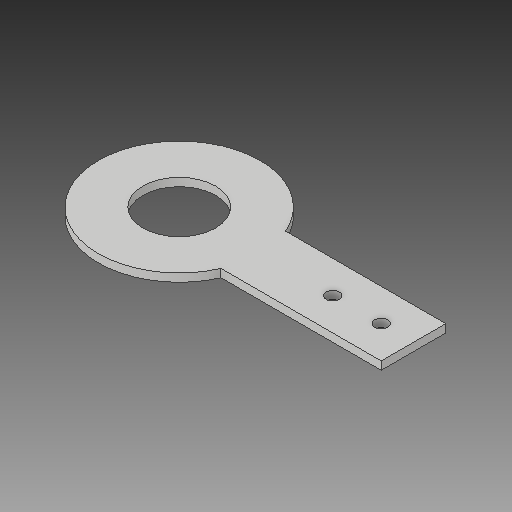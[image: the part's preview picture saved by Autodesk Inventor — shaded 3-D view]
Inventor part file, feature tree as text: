
AUTODESK INVENTOR PART (.ipt)
format: ipt  version: 2018 (Build 220112000, 112)  size: 98,816 bytes
history: native  units: in
note: dims shown in document units (in); Inventor stores cm internally (conversion verified against a paired STEP export)
features: other x3, sketch x1
ambient origin geometry x8: Origin, YZ Plane, XZ Plane, XY Plane, X Axis, Y Axis, Z Axis, Center Point
bodies: Solid1 (feature_tree)
feature tree (4):
  other  "wheel tip.ipt"
  other  "Solid1::wheel tip.ipt"
  other  "TaggingFeature1"
  sketch  "Sketch1"  dims[d0=0.3937in]
